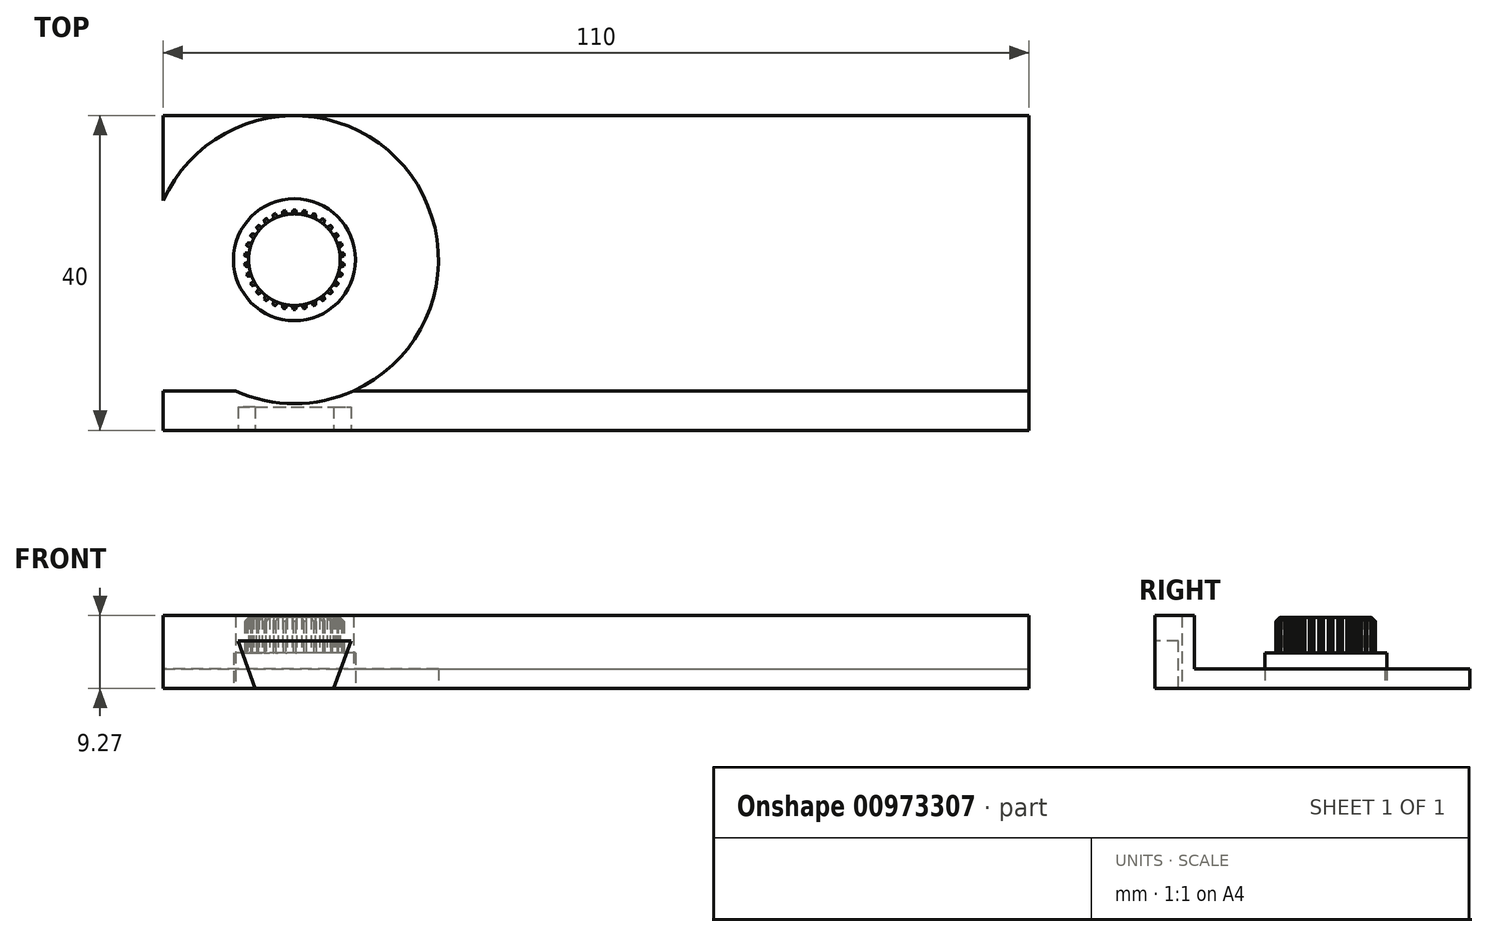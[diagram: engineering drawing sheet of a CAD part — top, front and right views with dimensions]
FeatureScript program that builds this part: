
annotation { "Feature Type Name" : "Feature", "Feature Type Description" : "" }
export const myFeature = defineFeature(function(context is Context, id is Id, definition is map)
    precondition{}
    {
        {
            var Q0;
            Q0=qCreatedBy(makeId("Top.planeOp"),FACE);
            var sketch = newSketch(context, id + "F0", { "sketchPlane" : qUnion([Q0])});
            skLineSegment(sketch, "E0.bottom", {"start": v(-55, 18.31) * mm, "end": v(55, 18.31) * mm});
            skLineSegment(sketch, "E0.top", {"start": v(-55, -21.69) * mm, "end": v(55, -21.69) * mm});
            skLineSegment(sketch, "E0.left", {"start": v(-55, 18.31) * mm, "end": v(-55, -21.69) * mm});
            skLineSegment(sketch, "E0.right", {"start": v(55, 18.31) * mm, "end": v(55, -21.69) * mm});
            skCircle(sketch, "E1", {"center": v(-38.31, 0) * mm, "radius": 14.29 * mm, "construction": true});
            skLineSegment(sketch, "E2", {"start": v(-55, -16.69) * mm, "end": v(55, -16.69) * mm});
            skCircle(sketch, "E3", {"center": v(-38.31, 0) * mm, "radius": 7.75 * mm});
            skCircle(sketch, "E4", {"center": v(-38.31, 0) * mm, "radius": 6.33 * mm});
            skCircle(sketch, "E5", {"center": v(-38.31, 0) * mm, "radius": 5.83 * mm});
            skLineSegment(sketch, "E6", {"start": v(-32, 0.5) * mm, "end": v(-32.5, 0.32) * mm});
            skLineSegment(sketch, "E7.MirrorCS", {"start": v(-32, -0.5) * mm, "end": v(-32.5, -0.32) * mm});
            skCircle(sketch, "E8", {"center": v(-38.31, 0) * mm, "radius": 16.29 * mm});
            skCircle(sketch, "E9", {"center": v(-38.31, 0) * mm, "radius": 18.29 * mm});
            skSolve(sketch);
        }
        {
            var Q0;
            {var subQ2=sQuery(id+"F0.wireOp",EDGE,"E0.bottom");Q0=makeQuery(id+"F0.imprint","IMPRINT",FACE,{"disambiguationData":[TD([[makeQuery(id+"F0.imprint","IMPRINT",EDGE,{"derivedFrom":subQ2}),-1.0]])]});}
            extrude(context, id + "F1", {"entities" : qUnion([Q0]), "depth" : 2.5 * mm, "offsetDistance" : 25 * mm});
        }
        {
            var Q0;
            Q0=makeQuery(id+"F0.imprint","IMPRINT",FACE,{"disambiguationData":[TD([[makeQuery(id+"F0.imprint","IMPRINT",EDGE,{"derivedFrom":sQuery(id+"F0.wireOp",EDGE,"E3")}),1.0]])]});
            extrude(context, id + "F2", {"entities" : qUnion([Q0]), "operationType" : NewBodyOperationType.ADD, "depth" : 4.5 * mm, "offsetDistance" : 25 * mm});
        }
        {
            var Q0;
            Q0=makeQuery(id+"F0.imprint","IMPRINT",FACE,{"disambiguationData":[TD([[makeQuery(id+"F0.imprint","IMPRINT",EDGE,{"derivedFrom":sQuery(id+"F0.wireOp",EDGE,"E4")}),1.0]])]});
            var Q1;
            {var subQ0=sQuery(id+"F0.wireOp",EDGE,"E5");var subQ1=makeQuery(id+"F0.imprint","INTERSECT",VERTEX,{"derivedFrom":[subQ0,sQuery(id+"F0.wireOp",EDGE,"E6")]});Q1=makeQuery(id+"F0.imprint","IMPRINT",FACE,{"disambiguationData":[TD([[makeQuery(id+"F0.imprint","IMPRINT",EDGE,{"disambiguationData":[TD([[subQ1,-1.0]])],"derivedFrom":subQ0}),1.0]])]});}
            extrude(context, id + "F3", {"entities" : qUnion([Q0, Q1]), "operationType" : NewBodyOperationType.ADD, "depth" : 9 * mm, "offsetDistance" : 25 * mm});
        }
        {
            var Q0;
            {var subQ0=sQuery(id+"F0.wireOp",EDGE,"E0.top");Q0=makeQuery(id+"F0.imprint","IMPRINT",FACE,{"disambiguationData":[TD([[makeQuery(id+"F0.imprint","IMPRINT",EDGE,{"derivedFrom":subQ0}),1.0]])]});}
            extrude(context, id + "F4", {"entities" : qUnion([Q0]), "operationType" : NewBodyOperationType.ADD, "depth" : 9.27 * mm, "offsetDistance" : 25 * mm});
        }
        {
            var Q0;
            Q0=makeQuery(id+"F3.opExtrude","CAP_EDGE",EDGE,{"disambiguationData":[OSD([sQuery(id+"F0.wireOp",EDGE,"E4")])],"isStart":false});
            chamfer(context, id + "F5", {"entities" : qUnion([Q0]), "width" : .5 * mm, "tangentPropagation" : true});
        }
        {
            var Q0;
            {var subQ0=sQuery(id+"F0.wireOp",EDGE,"E6");Q0=makeQuery(id+"F0.imprint","IMPRINT",FACE,{"disambiguationData":[TD([[makeQuery(id+"F0.imprint","IMPRINT",EDGE,{"derivedFrom":subQ0}),1.0]])]});}
            extrude(context, id + "F6", {"entities" : qUnion([Q0]), "operationType" : NewBodyOperationType.REMOVE, "depth" : 9 * mm, "offsetDistance" : 25 * mm, "hasSecondDirection" : true, "secondDirectionOppositeDirection" : false, "secondDirectionDepth" : 4.5 * mm});
        }
        {
            var Q0;
            Q0=makeQuery(id+"F6.boolean.opBoolean","COPY",FACE,{"derivedFrom":makeQuery(id+"F6.opExtrude","SWEPT_FACE",FACE,{"disambiguationData":[OSD([sQuery(id+"F0.wireOp",EDGE,"E5")])]})});
            var Q1;
            Q1=makeQuery(id+"F6.boolean.opBoolean","COPY",FACE,{"derivedFrom":makeQuery(id+"F6.opExtrude","SWEPT_FACE",FACE,{"disambiguationData":[OSD([sQuery(id+"F0.wireOp",EDGE,"E6")])]})});
            var Q2;
            Q2=makeQuery(id+"F6.boolean.opBoolean","COPY",FACE,{"derivedFrom":makeQuery(id+"F6.opExtrude","SWEPT_FACE",FACE,{"disambiguationData":[OSD([sQuery(id+"F0.wireOp",EDGE,"E7.MirrorCS")])]})});
            var Q3;
            Q3=makeQuery(id+"F3.opExtrude","SWEPT_FACE",FACE,{"disambiguationData":[OSD([sQuery(id+"F0.wireOp",EDGE,"E4")])]});
            circularPattern(context, id + "F7", {"patternType" : PatternType.FACE, "faces" : qUnion([Q0, Q1, Q2]), "axis" : qUnion([Q3]), "angle" : 360 * degree, "instanceCount" : 30, "equalSpace" : true});
        }
        {
            var Q0;
            Q0=makeQuery(id+"F4.opExtrude","SWEPT_FACE",FACE,{"disambiguationData":[OSD([sQuery(id+"F0.wireOp",EDGE,"E0.top")])]});
            var sketch = newSketch(context, id + "F8", { "sketchPlane" : qUnion([Q0])});
            skLineSegment(sketch, "E10", {"start": v(-38.31, 9.27) * mm, "end": v(-38.31, 0) * mm, "construction": true});
            skLineSegment(sketch, "E11.bottom", {"start": v(-43.31, 0) * mm, "end": v(-33.31, 0) * mm});
            skLineSegment(sketch, "E11.top", {"start": v(-43.31, 6) * mm, "end": v(-33.31, 6) * mm});
            skLineSegment(sketch, "E11.left", {"start": v(-43.31, 0) * mm, "end": v(-43.31, 6) * mm});
            skLineSegment(sketch, "E11.right", {"start": v(-33.31, 0) * mm, "end": v(-33.31, 6) * mm});
            skLineSegment(sketch, "E12", {"start": v(-43.31, 0) * mm, "end": v(-45.5, 6) * mm});
            skLineSegment(sketch, "E13", {"start": v(-43.31, 6) * mm, "end": v(-45.5, 6) * mm});
            skLineSegment(sketch, "E14.MirrorCS", {"start": v(-33.31, 0) * mm, "end": v(-31.13, 6) * mm});
            skLineSegment(sketch, "E15.MirrorCS", {"start": v(-33.31, 6) * mm, "end": v(-31.13, 6) * mm});
            skSolve(sketch);
        }
        {
            var Q0;
            Q0=makeQuery(id+"F8.imprint","IMPRINT",FACE,{"disambiguationData":[TD([[makeQuery(id+"F8.imprint","IMPRINT",EDGE,{"derivedFrom":sQuery(id+"F8.wireOp",EDGE,"E11.right")}),-1.0]])]});
            var Q1;
            Q1=makeQuery(id+"F8.imprint","IMPRINT",FACE,{"disambiguationData":[TD([[makeQuery(id+"F8.imprint","IMPRINT",EDGE,{"derivedFrom":sQuery(id+"F8.wireOp",EDGE,"E11.bottom")}),1.0]])]});
            var Q2;
            Q2=makeQuery(id+"F8.imprint","IMPRINT",FACE,{"disambiguationData":[TD([[makeQuery(id+"F8.imprint","IMPRINT",EDGE,{"derivedFrom":sQuery(id+"F8.wireOp",EDGE,"E11.left")}),1.0]])]});
            extrude(context, id + "F9", {"entities" : qUnion([Q0, Q1, Q2]), "operationType" : NewBodyOperationType.REMOVE, "oppositeDirection" : true, "depth" : 3 * mm, "offsetDistance" : 25 * mm});
        }
    });
